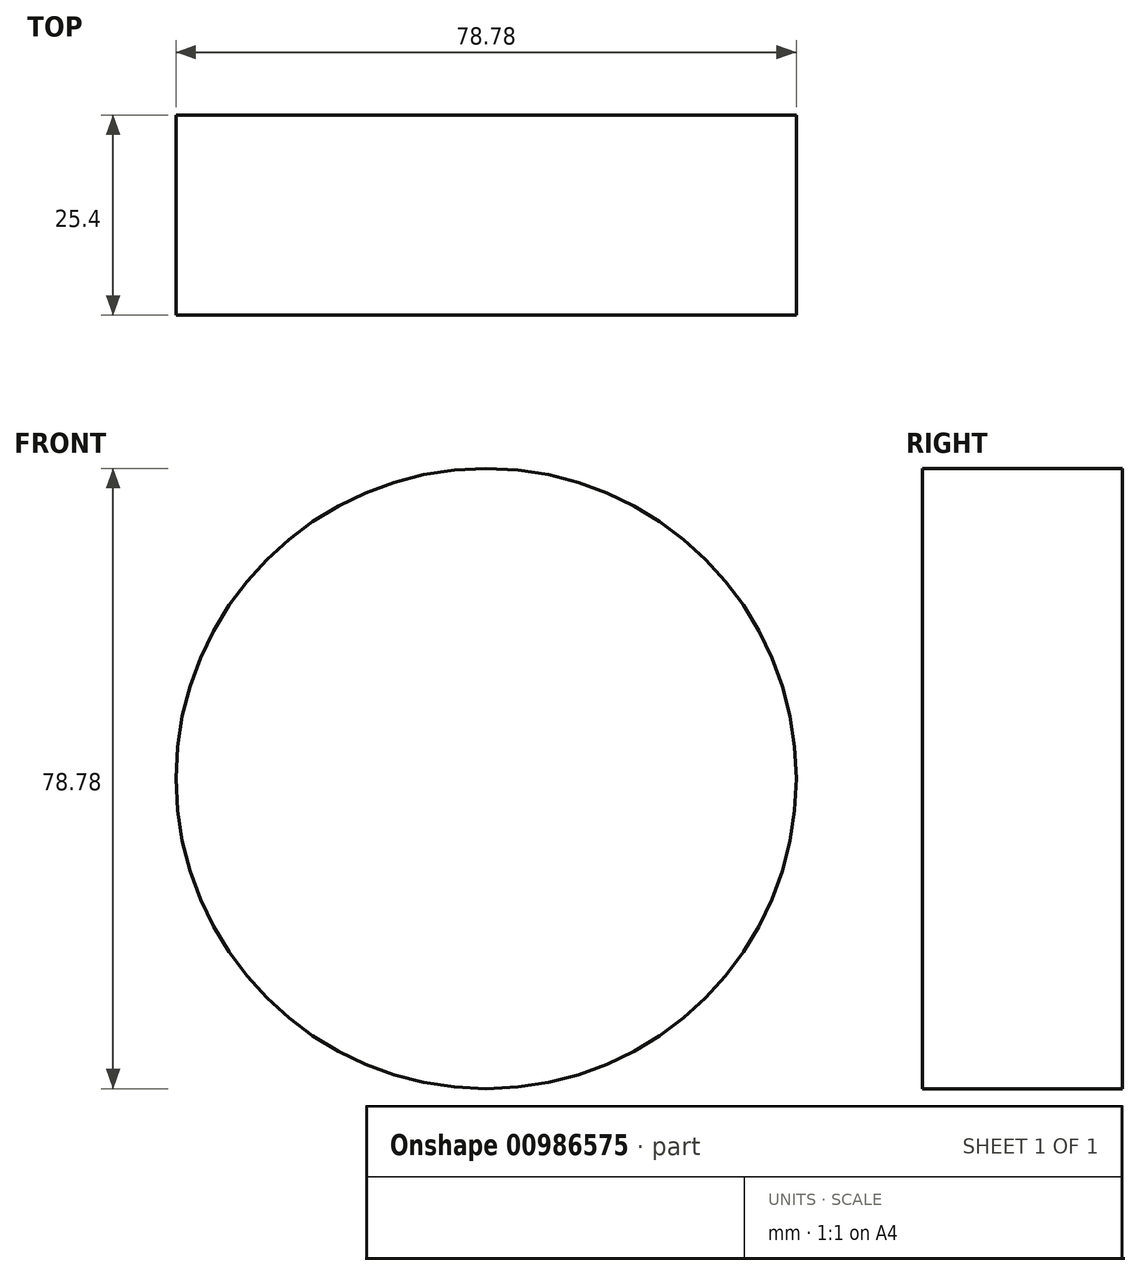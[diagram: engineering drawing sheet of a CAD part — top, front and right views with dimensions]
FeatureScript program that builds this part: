
annotation { "Feature Type Name" : "Feature", "Feature Type Description" : "" }
export const myFeature = defineFeature(function(context is Context, id is Id, definition is map)
    precondition{}
    {
        {
            var Q0;
            Q0=qCreatedBy(makeId("Front.planeOp"),FACE);
            var sketch = newSketch(context, id + "F0", { "sketchPlane" : qUnion([Q0])});
            skCircle(sketch, "E0", {"center": v(0, 0) * mm, "radius": 39.4 * mm});
            skSolve(sketch);
        }
        {
            var Q0;
            Q0 = qSketchRegion(id + "F0", true);
            extrude(context, id + "F1", {"entities" : qUnion([Q0]), "depth" : 25.4 * mm, "offsetDistance" : 25.4 * mm});
        }
    });
